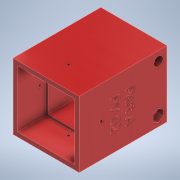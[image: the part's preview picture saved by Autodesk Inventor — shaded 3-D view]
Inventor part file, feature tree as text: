
AUTODESK INVENTOR PART (.ipt)
format: ipt  version: 2022.1 (Build 261234000, 234)  size: 438,272 bytes
history: native  units: mm
features: sketch x16, extrude x8, plane x3, hole x3, loft x2, emboss x1, projected_geometry x1
ambient origin geometry x8: Origin, YZ Plane, XZ Plane, XY Plane, X Axis, Y Axis, Z Axis, Center Point
bodies: Body1 (feature_tree)
feature tree (34):
  extrude  "Extrusion12"  Depth=51.5mm
  extrude  "Extrusion13"  Depth=4.0mm
  sketch  "Sketch18"  dims[d91=25.0mm d92=0.0mm d93=46.5mm]
  plane  "Work Plane3"
  extrude  "Extrusion16"  Depth=46.5mm
  loft  "Loft1"
  hole  "Hole4"  [1 undecoded]
  hole  "Hole5"  [1 undecoded]
  plane  "Work Plane4"
  extrude  "Extrusion17"  Depth=5.0mm
  loft  "Loft2"
  plane  "Work Plane5"
  hole  "Hole6"  [1 undecoded]
  extrude  "Extrusion18"  Depth=5.0mm
  extrude  "Extrusion19"  TaperAngle=0.0deg  [1 undecoded]
  extrude  "Extrusion20"  Depth=7.5mm
  extrude  "Extrusion21"  Depth=8.0mm
  emboss  "Emboss3"
  sketch  "Sketch15"  dims[d87=51.5mm d88=51.5mm]
  sketch  "Sketch16"  dims[d89=4.0mm d90=4.0mm]
  sketch  "Sketch21"  dims[d94=46.5mm d95=34.0mm d96=0.0mm]
  sketch  "Sketch22"  dims[d106=0.0mm d107=15.0mm d108=0.0mm d109=6.0mm]
  sketch  "Sketch23"  dims[d110=25.0mm d111=0.0mm d112=90.0deg]
  sketch  "Sketch24"  dims[d113=0.0mm d114=90.0deg d118=5.0mm]
  sketch  "Sketch25"  dims[d119=2.705mm d120=6.0mm d121=4.369mm d122=2.0mm d123=14.3117mm d124=8.0mm d125=20.594885mm d126=5.0mm]
  sketch  "Sketch26"  dims[d127=2.705mm d128=6.0mm d129=4.0mm d130=2.0mm d131=90.0deg d132=8.0mm d133=20.594885mm d134=0.0mm]
  projected_geometry  "Projected Loop1"
  sketch  "Sketch27"  dims[d135=5.0mm d136=0.0mm d137=5.0mm]
  sketch  "Sketch28"  dims[d138=0.0mm d139=90.0deg d140=0.0mm d141=90.0deg]
  sketch  "Sketch29"  dims[d142=7.5mm d143=7.5mm]
  sketch  "Sketch30"  dims[d146=4.915mm d147=6.0mm d148=8.433mm d149=2.0mm d150=14.3117mm d151=8.0mm d152=20.594885mm d153=8.625mm]
  sketch  "Sketch31"  dims[d154=8.625mm]
  sketch  "Sketch32"  dims[d155=8.255mm]
  sketch  "Sketch33"  dims[d156=6.858mm d157=0.0mm d158=8.255mm d159=6.858mm d160=0.0mm d161=9.23925mm d162=6.858mm d163=0.0mm d164=9.23925mm d165=6.858mm d166=0.0mm d167=1.0mm d168=0.0mm]
note: 4 required parameter values undecoded (feature->parameter linkage not recoverable at this tier; creation-order binding heuristic only, values carry confidence <= 0.55)
